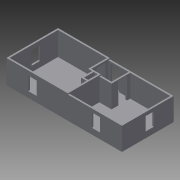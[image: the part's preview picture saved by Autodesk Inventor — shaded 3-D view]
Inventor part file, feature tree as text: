
AUTODESK INVENTOR PART (.ipt)
format: ipt  version: 2013 SP2 (Build 170200200, 200)  size: 269,312 bytes
history: native  units: in
note: dims shown in document units (in); Inventor stores cm internally (conversion verified against a paired STEP export)
features: extrude x8, sketch x5, projected_geometry x3, mirror x1
ambient origin geometry x8: Origin, YZ Plane, XZ Plane, XY Plane, X Axis, Y Axis, Z Axis, Center Point
feature tree (17):
  extrude  "Extrusion12"  Depth=434.0in
  extrude  "Extrusion13"  Depth=6.0in
  sketch  "Sketch11"  dims[d17=57.0in d18=79.0in d19=6.0in d20=6.0in d21=6.0in]
  extrude  "Extrusion15"  Depth=6.0in
  extrude  "Extrusion16"  Depth=120.0in
  extrude  "Extrusion17"  Depth=222.0in
  extrude  "Extrusion18"  Depth=6.0in
  extrude  "Extrusion19"  Depth=70.0in
  mirror  "Mirror3"
  extrude  "Extrusion20"  Depth=12.0in
  sketch  "Sketch1"  dims[d0=6.0in d1=183.0in d8=6.0in d12=434.0in]
  sketch  "Sketch10"  dims[d13=170.0in d14=6.0in d15=6.0in]
  projected_geometry  "Projected Loop2"
  sketch  "Sketch12"  dims[d22=151.0in d23=199.0in d24=120.0in d25=6.0in d26=51.0in]
  projected_geometry  "Projected Loop3"
  sketch  "Sketch13"  dims[d27=6.0in d28=222.0in d29=194.0in d30=6.0in d31=70.0in d32=198.0in d33=12.0in d34=44.0in d35=12.0in d36=44.0in d37=6.0in d38=151.0in d40=6.0in d41=32.0in d42=183.0in d73=6.0in d74=6.0in d75=6.0in d76=120.0in d77=112.0in d78=6.0in d79=219.0in d80=70.0in d81=84.0in d82=0.0in d83=1.0in d84=0.0in d87=3.0in d88=0.0in d89=4.0in d90=0.0in d91=4.0in d92=0.0in d93=74.0in d94=31.0in d95=13.0in d96=21.0in d97=4.0in d98=0.0in d99=82.0in d100=31.0in d101=13.0in d102=21.0in d103=4.0in d104=0.0in d105=8.0in d106=0.0in]
  projected_geometry  "Projected Loop4"
